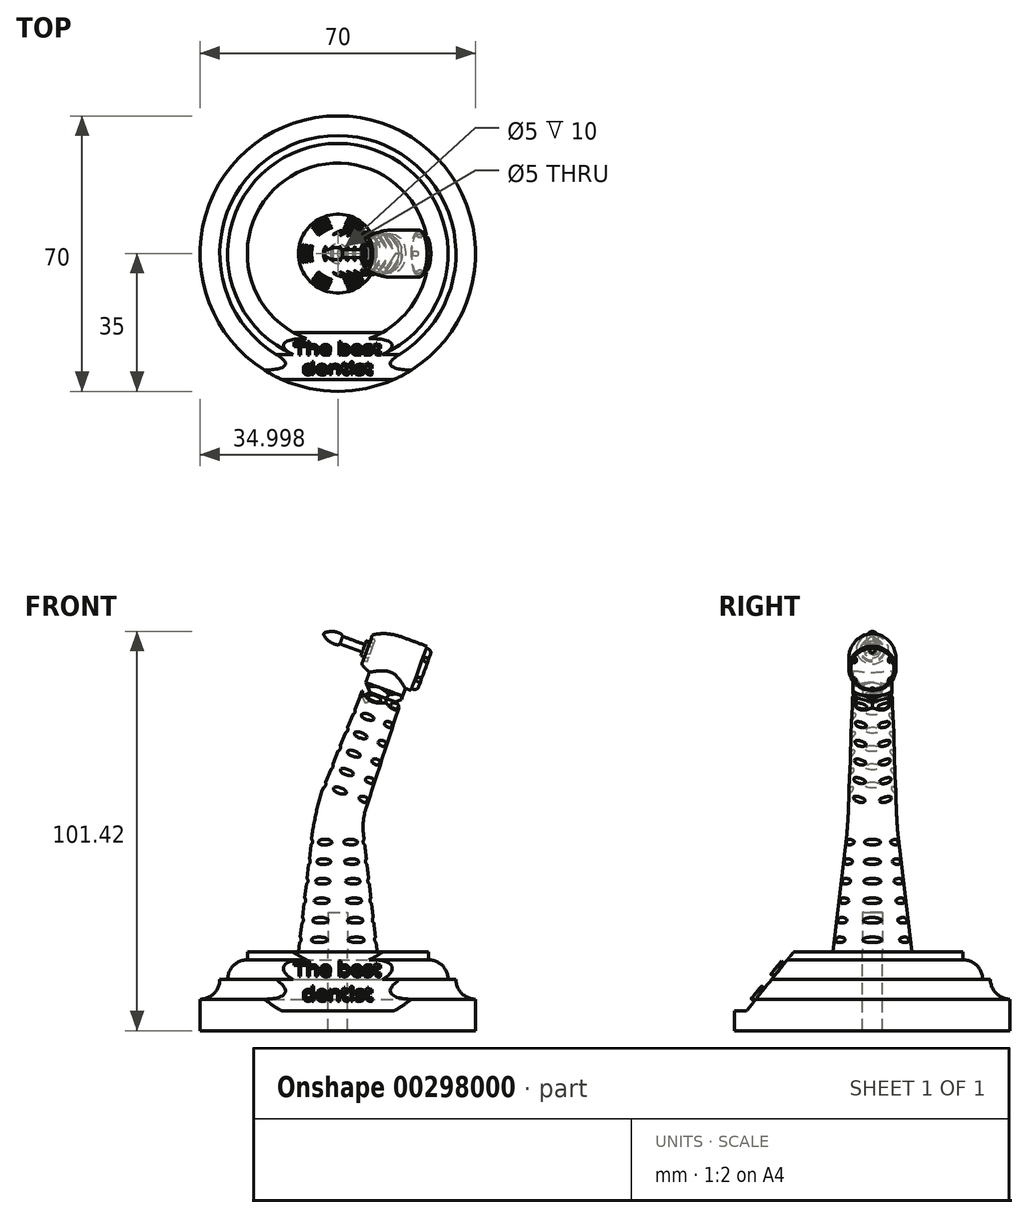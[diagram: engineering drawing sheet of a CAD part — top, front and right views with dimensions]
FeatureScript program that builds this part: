
annotation { "Feature Type Name" : "Feature", "Feature Type Description" : "" }
export const myFeature = defineFeature(function(context is Context, id is Id, definition is map)
    precondition{}
    {
        {
            var Q0;
            Q0=qCreatedBy(makeId("Front.planeOp"),FACE);
            var sketch = newSketch(context, id + "F0", { "sketchPlane" : qUnion([Q0])});
            skLineSegment(sketch, "E0.top", {"start": v(0, 6) * mm, "end": v(-7.07, 6) * mm});
            skArc(sketch, "E1", {"start": v(-7.07, 6) * mm, "mid": v(-10.68, 5.49) * mm, "end": v(-14, 4) * mm});
            skLineSegment(sketch, "E2", {"start": v(0, 6) * mm, "end": v(0, 0) * mm});
            skLineSegment(sketch, "E3", {"start": v(-14, 4) * mm, "end": v(-14, 3) * mm});
            skLineSegment(sketch, "E4", {"start": v(-13, 0) * mm, "end": v(0, 0) * mm});
            skLineSegment(sketch, "E5", {"start": v(0, 5.5) * mm, "end": v(0.5, 5.5) * mm});
            skLineSegment(sketch, "E6", {"start": v(1.5, 4.5) * mm, "end": v(1.5, 0) * mm});
            skPoint(sketch, "E7.visualSharp", {"position": v(1.5, 5.5) * mm});
            skArc(sketch, "E7.filletArc", {"start": v(1.5, 4.5) * mm, "mid": v(1.2, 5.2) * mm, "end": v(0.5, 5.5) * mm});
            skLineSegment(sketch, "E8", {"start": v(1.5, 0) * mm, "end": v(0, 0) * mm});
            skLineSegment(sketch, "E9", {"start": v(-14, 3) * mm, "end": v(-13, 3) * mm});
            skLineSegment(sketch, "E10", {"start": v(-13, 3) * mm, "end": v(-13, 2) * mm});
            skLineSegment(sketch, "E11", {"start": v(-13, 2) * mm, "end": v(-15, 2) * mm});
            skLineSegment(sketch, "E12", {"start": v(-15, 2) * mm, "end": v(-15, 1) * mm});
            skLineSegment(sketch, "E13", {"start": v(-15, 1) * mm, "end": v(-13, 1) * mm});
            skLineSegment(sketch, "E14", {"start": v(-13, 1) * mm, "end": v(-13, 0) * mm});
            skLineSegment(sketch, "E15", {"start": v(-25.15, 0) * mm, "end": v(8.44, 0) * mm, "construction": true});
            skLineSegment(sketch, "E16", {"start": v(-6.5, 17.79) * mm, "end": v(-6.5, -18.93) * mm, "construction": true});
            skSolve(sketch);
        }
        {
            var Q0;
            {var subQ1=sQuery(id+"F0.wireOp",EDGE,"E0.top");Q0=makeQuery(id+"F0.imprint","IMPRINT",FACE,{"disambiguationData":[TD([[makeQuery(id+"F0.imprint","IMPRINT",EDGE,{"derivedFrom":subQ1}),1.0]])]});}
            var Q1;
            Q1=sQuery(id+"F0.wireOp",EDGE,"E15");
            revolve(context, id + "F1", {"entities" : qUnion([Q0]), "axis" : qUnion([Q1]), "revolveType" : RevolveType.FULL});
        }
        {
            var Q0;
            {var subQ0=sQuery(id+"F0.wireOp",EDGE,"E5");Q0=makeQuery(id+"F0.imprint","IMPRINT",FACE,{"disambiguationData":[TD([[makeQuery(id+"F0.imprint","IMPRINT",EDGE,{"derivedFrom":subQ0}),-1.0]])]});}
            var Q1;
            Q1=sQuery(id+"F0.wireOp",EDGE,"E15");
            revolve(context, id + "F2", {"entities" : qUnion([Q0]), "axis" : qUnion([Q1]), "revolveType" : RevolveType.FULL});
        }
        {
            var Q0;
            Q0=qCreatedBy(makeId("Front.planeOp"),FACE);
            var sketch = newSketch(context, id + "F3", { "sketchPlane" : qUnion([Q0])});
            skLineSegment(sketch, "E17", {"start": v(11.5, 0) * mm, "end": v(-3.06, 8.57) * mm, "construction": true});
            skArc(sketch, "E18.0", {"start": v(1.5, 4.5) * mm, "mid": v(1.2, 5.2) * mm, "end": v(0.5, 5.5) * mm, "construction": true});
            skLineSegment(sketch, "E19", {"start": v(0.5, 7.63) * mm, "end": v(3.95, 5.6) * mm});
            skLineSegment(sketch, "E20", {"start": v(3.95, 5.6) * mm, "end": v(3.45, 4.74) * mm});
            skLineSegment(sketch, "E21", {"start": v(3.45, 4.74) * mm, "end": v(0, 6.77) * mm});
            skLineSegment(sketch, "E22", {"start": v(0, 6.77) * mm, "end": v(0.5, 7.63) * mm});
            skSolve(sketch);
        }
        {
            var Q0;
            Q0 = qSketchRegion(id + "F3", true);
            var Q1;
            Q1=sQuery(id+"F3.wireOp",EDGE,"E17");
            revolve(context, id + "F4", {"entities" : qUnion([Q0]), "axis" : qUnion([Q1]), "revolveType" : RevolveType.FULL});
        }
        {
            var Q0;
            Q0=makeQuery(id+"F4.opRevolve","SWEPT_BODY",BODY,{"disambiguationData":[OSD([sQuery(id+"F3.wireOp",EDGE,"E19"),sQuery(id+"F3.wireOp",EDGE,"E20"),sQuery(id+"F3.wireOp",EDGE,"E21"),sQuery(id+"F3.wireOp",EDGE,"E22")])]});
            var Q1;
            Q1=sQuery(id+"F0.wireOp",EDGE,"E15");
            circularPattern(context, id + "F5", {"entities" : qUnion([Q0]), "axis" : qUnion([Q1]), "angle" : 360 * degree, "instanceCount" : 6, "equalSpace" : true});
        }
        {
            var Q0;
            Q0=makeQuery(id+"F4.opRevolve","SWEPT_BODY",BODY,{"disambiguationData":[OSD([sQuery(id+"F3.wireOp",EDGE,"E19"),sQuery(id+"F3.wireOp",EDGE,"E20"),sQuery(id+"F3.wireOp",EDGE,"E21"),sQuery(id+"F3.wireOp",EDGE,"E22")])]});
            var Q1;
            Q1=makeQuery(id+"F5.opPattern","COPY",BODY,{"derivedFrom":makeQuery(id+"F4.opRevolve","SWEPT_BODY",BODY,{"disambiguationData":[OSD([sQuery(id+"F3.wireOp",EDGE,"E19"),sQuery(id+"F3.wireOp",EDGE,"E20"),sQuery(id+"F3.wireOp",EDGE,"E21"),sQuery(id+"F3.wireOp",EDGE,"E22")])]}),"instanceName":"4"});
            var Q2;
            Q2=makeQuery(id+"F5.opPattern","COPY",BODY,{"derivedFrom":makeQuery(id+"F4.opRevolve","SWEPT_BODY",BODY,{"disambiguationData":[OSD([sQuery(id+"F3.wireOp",EDGE,"E19"),sQuery(id+"F3.wireOp",EDGE,"E20"),sQuery(id+"F3.wireOp",EDGE,"E21"),sQuery(id+"F3.wireOp",EDGE,"E22")])]}),"instanceName":"3"});
            var Q3;
            Q3=makeQuery(id+"F5.opPattern","COPY",BODY,{"derivedFrom":makeQuery(id+"F4.opRevolve","SWEPT_BODY",BODY,{"disambiguationData":[OSD([sQuery(id+"F3.wireOp",EDGE,"E19"),sQuery(id+"F3.wireOp",EDGE,"E20"),sQuery(id+"F3.wireOp",EDGE,"E21"),sQuery(id+"F3.wireOp",EDGE,"E22")])]}),"instanceName":"2"});
            var Q4;
            Q4=makeQuery(id+"F5.opPattern","COPY",BODY,{"derivedFrom":makeQuery(id+"F4.opRevolve","SWEPT_BODY",BODY,{"disambiguationData":[OSD([sQuery(id+"F3.wireOp",EDGE,"E19"),sQuery(id+"F3.wireOp",EDGE,"E20"),sQuery(id+"F3.wireOp",EDGE,"E21"),sQuery(id+"F3.wireOp",EDGE,"E22")])]}),"instanceName":"1"});
            var Q5;
            Q5=makeQuery(id+"F5.opPattern","COPY",BODY,{"derivedFrom":makeQuery(id+"F4.opRevolve","SWEPT_BODY",BODY,{"disambiguationData":[OSD([sQuery(id+"F3.wireOp",EDGE,"E19"),sQuery(id+"F3.wireOp",EDGE,"E20"),sQuery(id+"F3.wireOp",EDGE,"E21"),sQuery(id+"F3.wireOp",EDGE,"E22")])]}),"instanceName":"5"});
            var Q6;
            Q6=makeQuery(id+"F2.opRevolve","SWEPT_BODY",BODY,{"disambiguationData":[OSD([sQuery(id+"F0.wireOp",EDGE,"E2"),sQuery(id+"F0.wireOp",EDGE,"E5"),sQuery(id+"F0.wireOp",EDGE,"E6"),sQuery(id+"F0.wireOp",EDGE,"E7.filletArc"),sQuery(id+"F0.wireOp",EDGE,"E8")])]});
            booleanBodies(context, id + "F6", {"operationType" : BooleanOperationType.SUBTRACTION, "tools" : qUnion([Q0, Q1, Q2, Q3, Q4, Q5]), "targets" : qUnion([Q6])});
        }
        {
            var Q0;
            Q0=qCreatedBy(makeId("Front.planeOp"),FACE);
            var sketch = newSketch(context, id + "F7", { "sketchPlane" : qUnion([Q0])});
            skLineSegment(sketch, "E23.0", {"start": v(-25.15, 0) * mm, "end": v(8.44, 0) * mm, "construction": true});
            skPoint(sketch, "E24.0", {"position": v(-13, 1) * mm});
            skLineSegment(sketch, "E25", {"start": v(-13, 1) * mm, "end": v(-21, 1) * mm});
            skArc(sketch, "E26", {"start": v(-21.74, 1.5) * mm, "mid": v(-23.76, 1.33) * mm, "end": v(-25.55, 0.39) * mm});
            skArc(sketch, "E27", {"start": v(-21, 1) * mm, "mid": v(-21.31, 1.33) * mm, "end": v(-21.74, 1.5) * mm});
            skArc(sketch, "E28", {"start": v(-25.55, 0.39) * mm, "mid": v(-25.69, 0.21) * mm, "end": v(-25.73, 0) * mm});
            skLineSegment(sketch, "E29", {"start": v(-25.73, 0) * mm, "end": v(-13, 0) * mm});
            skLineSegment(sketch, "E30", {"start": v(-13, 0) * mm, "end": v(-13, 1) * mm});
            skSolve(sketch);
        }
        {
            var Q0;
            Q0 = qSketchRegion(id + "F7", true);
            var Q1;
            Q1=sQuery(id+"F7.wireOp",EDGE,"E23.0");
            revolve(context, id + "F8", {"entities" : qUnion([Q0]), "axis" : qUnion([Q1]), "revolveType" : RevolveType.FULL});
        }
        {
            var Q0;
            Q0=qCreatedBy(makeId("Top.planeOp"),FACE);
            cPlane(context, id + "F9", {"entities" : qUnion([Q0]), "cplaneType" : CPlaneType.OFFSET, "offset" : 6 * mm, "oppositeDirection" : true, "width" : 150 * mm, "height" : 150 * mm});
        }
        {
            var Q0;
            Q0=qCreatedBy(id+"F9.planeOp",FACE);
            var sketch = newSketch(context, id + "F10", { "sketchPlane" : qUnion([Q0])});
            skPoint(sketch, "E31.0", {"position": v(-6.5, 0) * mm});
            skCircle(sketch, "E32", {"center": v(-6.5, 0) * mm, "radius": 5 * mm});
            skSolve(sketch);
        }
        {
            var Q0;
            Q0 = qSketchRegion(id + "F10", true);
            extrude(context, id + "F11", {"entities" : qUnion([Q0]), "operationType" : NewBodyOperationType.ADD, "depth" : 5 * mm, "hasSecondDirection" : true, "secondDirectionOppositeDirection" : true, "secondDirectionDepth" : 2 * mm});
        }
        {
            var Q0;
            Q0=qCreatedBy(makeId("Front.planeOp"),FACE);
            var sketch = newSketch(context, id + "F12", { "sketchPlane" : qUnion([Q0])});
            skLineSegment(sketch, "E33", {"start": v(-6.5, 12.02) * mm, "end": v(-6.5, -38) * mm, "construction": true});
            skLineSegment(sketch, "E34", {"start": v(-11.5, -8) * mm, "end": v(-12.5, -38) * mm});
            skLineSegment(sketch, "E35.0", {"start": v(-11.5, -8) * mm, "end": v(-1.5, -8) * mm});
            skLineSegment(sketch, "E36", {"start": v(-6.5, -38) * mm, "end": v(-6.5, -8) * mm});
            skLineSegment(sketch, "E37", {"start": v(-12.5, -38) * mm, "end": v(-0.5, -38) * mm});
            skLineSegment(sketch, "E38", {"start": v(-5, -46.55) * mm, "end": v(38.76, -166.76) * mm, "construction": true});
            skLineSegment(sketch, "E39", {"start": v(5.27, -74.74) * mm, "end": v(-4.13, -78.16) * mm});
            skLineSegment(sketch, "E40", {"start": v(-11.1, -48.77) * mm, "end": v(1.12, -44.33) * mm});
            skPoint(sketch, "E41", {"position": v(-5, -46.55) * mm});
            skLineSegment(sketch, "E42", {"start": v(-11.1, -48.77) * mm, "end": v(-4.13, -78.16) * mm});
            skLineSegment(sketch, "E43", {"start": v(-5, -46.55) * mm, "end": v(5.27, -74.74) * mm});
            skArc(sketch, "E44", {"start": v(-6.5, -38) * mm, "mid": v(-6.12, -42.34) * mm, "end": v(-5, -46.55) * mm});
            skSolve(sketch);
        }
        {
            var Q0;
            {var subQ0=sQuery(id+"F12.wireOp",EDGE,"E34");Q0=makeQuery(id+"F12.imprint","IMPRINT",FACE,{"disambiguationData":[TD([[makeQuery(id+"F12.imprint","IMPRINT",EDGE,{"derivedFrom":subQ0}),1.0]])]});}
            var Q1;
            Q1=sQuery(id+"F12.wireOp",EDGE,"E33");
            revolve(context, id + "F13", {"operationType" : NewBodyOperationType.ADD, "entities" : qUnion([Q0]), "axis" : qUnion([Q1]), "revolveType" : RevolveType.FULL});
        }
        {
            var Q0;
            Q0=makeQuery(id+"F12.imprint","IMPRINT",FACE,{"disambiguationData":[TD([[makeQuery(id+"F12.imprint","IMPRINT",EDGE,{"derivedFrom":sQuery(id+"F12.wireOp",EDGE,"E39")}),-1.0]])]});
            var Q1;
            Q1=makeQuery(id+"F12.imprint","IMPRINT",FACE,{"disambiguationData":[TD([[makeQuery(id+"F12.imprint","IMPRINT",EDGE,{"derivedFrom":sQuery(id+"F12.wireOp",EDGE,"E39")}),1.0]])]});
            var Q2;
            Q2=sQuery(id+"F12.wireOp",EDGE,"E38");
            revolve(context, id + "F14", {"entities" : qUnion([Q0, Q1]), "axis" : qUnion([Q2]), "revolveType" : RevolveType.FULL});
        }
        {
            var Q2;
            Q2=makeQuery(id+"F13.opRevolve","SWEPT_FACE",FACE,{"disambiguationData":[OSD([sQuery(id+"F12.wireOp",EDGE,"E37")])]});
            var Q3;
            Q3=makeQuery(id+"F14.opRevolve","SWEPT_FACE",FACE,{"disambiguationData":[OSD([sQuery(id+"F12.wireOp",EDGE,"E40")])]});
            loft(context, id + "F15", {"operationType" : NewBodyOperationType.ADD, "startCondition" : LoftEndDerivativeType.MATCH_TANGENT, "startMagnitude" : 1, "endCondition" : LoftEndDerivativeType.MATCH_TANGENT, "endMagnitude" : 1, "sheetProfilesArray" : [{ "sheetProfileEntities" : qUnion([Q2]) }, { "sheetProfileEntities" : qUnion([Q3]) }]});
        }
        {
            var Q0;
            Q0=qCreatedBy(makeId("Front.planeOp"),FACE);
            var sketch = newSketch(context, id + "F16", { "sketchPlane" : qUnion([Q0])});
            skLineSegment(sketch, "E45.0", {"start": v(-11.5, -8) * mm, "end": v(-12.5, -38) * mm, "construction": true});
            skLineSegment(sketch, "E45.1", {"start": v(-11.1, -48.77) * mm, "end": v(-4.13, -78.16) * mm, "construction": true});
            skLineSegment(sketch, "E46", {"start": v(-12.16, -6.94) * mm, "end": v(-13.27, -40.1) * mm, "construction": true});
            skCircle(sketch, "E47", {"center": v(-13.13, -36) * mm, "radius": 1 * mm});
            skCircle(sketch, "E48", {"center": v(-12.97, -31) * mm, "radius": 1 * mm});
            skCircle(sketch, "E49", {"center": v(-12.8, -26) * mm, "radius": 1 * mm});
            skCircle(sketch, "E50", {"center": v(-12.63, -21) * mm, "radius": 1 * mm});
            skLineSegment(sketch, "E51", {"start": v(-11.5, -8) * mm, "end": v(-9.57, -10) * mm});
            skLineSegment(sketch, "E52", {"start": v(-9.57, -10) * mm, "end": v(-11.63, -12) * mm});
            skLineSegment(sketch, "E53", {"start": v(-11.63, -12) * mm, "end": v(-11.5, -8) * mm});
            skCircle(sketch, "E54", {"center": v(-12.47, -16.01) * mm, "radius": 1 * mm});
            skLineSegment(sketch, "E55", {"start": v(-12.52, -45.84) * mm, "end": v(-4.54, -79.46) * mm, "construction": true});
            skCircle(sketch, "E56", {"center": v(-11.3, -50.97) * mm, "radius": 1 * mm});
            skCircle(sketch, "E57", {"center": v(-10.14, -55.84) * mm, "radius": 1 * mm});
            skCircle(sketch, "E58", {"center": v(-8.99, -60.7) * mm, "radius": 1 * mm});
            skCircle(sketch, "E59", {"center": v(-7.84, -65.57) * mm, "radius": 1 * mm});
            skCircle(sketch, "E60", {"center": v(-6.68, -70.43) * mm, "radius": 1 * mm});
            skCircle(sketch, "E61", {"center": v(-5.53, -75.3) * mm, "radius": 1 * mm});
            skCircle(sketch, "E62", {"center": v(-12.3, -11.01) * mm, "radius": 1 * mm});
            skSolve(sketch);
        }
        {
            var Q0;
            {var subQ1=sQuery(id+"F16.wireOp",EDGE,"E51");Q0=makeQuery(id+"F16.imprint","IMPRINT",FACE,{"disambiguationData":[TD([[makeQuery(id+"F16.imprint","IMPRINT",EDGE,{"derivedFrom":subQ1}),-1.0]])]});}
            var Q1;
            {var subQ0=sQuery(id+"F16.wireOp",EDGE,"E62");var subQ1=sQuery(id+"F16.wireOp",EDGE,"E53");var subQ2=makeQuery(id+"F16.imprint","INTERSECT",VERTEX,{"disambiguationData":[OD(0.0)],"derivedFrom":[subQ1,subQ0]});Q1=makeQuery(id+"F16.imprint","IMPRINT",FACE,{"disambiguationData":[TD([[makeQuery(id+"F16.imprint","IMPRINT",EDGE,{"disambiguationData":[TD([[subQ2,-1.0]])],"derivedFrom":subQ1}),-1.0]])]});}
            extrude(context, id + "F17", {"entities" : qUnion([Q0, Q1]), "operationType" : NewBodyOperationType.REMOVE, "endBound" : BoundingType.SYMMETRIC, "oppositeDirection" : true, "depth" : 25 * mm});
        }
        {
            var Q0;
            Q0=makeQuery(id+"F16.imprint","IMPRINT",FACE,{"disambiguationData":[TD([[makeQuery(id+"F16.imprint","IMPRINT",EDGE,{"derivedFrom":sQuery(id+"F16.wireOp",EDGE,"E54")}),1.0]])]});
            var Q1;
            Q1=makeQuery(id+"F16.imprint","IMPRINT",FACE,{"disambiguationData":[TD([[makeQuery(id+"F16.imprint","IMPRINT",EDGE,{"derivedFrom":sQuery(id+"F16.wireOp",EDGE,"E50")}),1.0]])]});
            var Q2;
            Q2=makeQuery(id+"F16.imprint","IMPRINT",FACE,{"disambiguationData":[TD([[makeQuery(id+"F16.imprint","IMPRINT",EDGE,{"derivedFrom":sQuery(id+"F16.wireOp",EDGE,"E49")}),1.0]])]});
            var Q3;
            Q3=makeQuery(id+"F16.imprint","IMPRINT",FACE,{"disambiguationData":[TD([[makeQuery(id+"F16.imprint","IMPRINT",EDGE,{"derivedFrom":sQuery(id+"F16.wireOp",EDGE,"E48")}),1.0]])]});
            var Q4;
            Q4=makeQuery(id+"F16.imprint","IMPRINT",FACE,{"disambiguationData":[TD([[makeQuery(id+"F16.imprint","IMPRINT",EDGE,{"derivedFrom":sQuery(id+"F16.wireOp",EDGE,"E47")}),1.0]])]});
            var Q5;
            Q5=makeQuery(id+"F16.imprint","IMPRINT",FACE,{"disambiguationData":[TD([[makeQuery(id+"F16.imprint","IMPRINT",EDGE,{"derivedFrom":sQuery(id+"F16.wireOp",EDGE,"E56")}),1.0]])]});
            var Q6;
            Q6=makeQuery(id+"F16.imprint","IMPRINT",FACE,{"disambiguationData":[TD([[makeQuery(id+"F16.imprint","IMPRINT",EDGE,{"derivedFrom":sQuery(id+"F16.wireOp",EDGE,"E57")}),1.0]])]});
            var Q7;
            Q7=makeQuery(id+"F16.imprint","IMPRINT",FACE,{"disambiguationData":[TD([[makeQuery(id+"F16.imprint","IMPRINT",EDGE,{"derivedFrom":sQuery(id+"F16.wireOp",EDGE,"E58")}),1.0]])]});
            var Q8;
            Q8=makeQuery(id+"F16.imprint","IMPRINT",FACE,{"disambiguationData":[TD([[makeQuery(id+"F16.imprint","IMPRINT",EDGE,{"derivedFrom":sQuery(id+"F16.wireOp",EDGE,"E59")}),1.0]])]});
            var Q9;
            Q9=makeQuery(id+"F16.imprint","IMPRINT",FACE,{"disambiguationData":[TD([[makeQuery(id+"F16.imprint","IMPRINT",EDGE,{"derivedFrom":sQuery(id+"F16.wireOp",EDGE,"E60")}),1.0]])]});
            var Q10;
            Q10=makeQuery(id+"F16.imprint","IMPRINT",FACE,{"disambiguationData":[TD([[makeQuery(id+"F16.imprint","IMPRINT",EDGE,{"derivedFrom":sQuery(id+"F16.wireOp",EDGE,"E61")}),1.0]])]});
            var Q11;
            {var subQ0=sQuery(id+"F16.wireOp",EDGE,"E62");var subQ1=sQuery(id+"F16.wireOp",EDGE,"E53");var subQ2=makeQuery(id+"F16.imprint","INTERSECT",VERTEX,{"disambiguationData":[OD(0.0)],"derivedFrom":[subQ1,subQ0]});Q11=makeQuery(id+"F16.imprint","IMPRINT",FACE,{"disambiguationData":[TD([[makeQuery(id+"F16.imprint","IMPRINT",EDGE,{"disambiguationData":[TD([[subQ2,-1.0]])],"derivedFrom":subQ1}),-1.0]])]});}
            var Q12;
            {var subQ0=sQuery(id+"F16.wireOp",EDGE,"E62");var subQ1=sQuery(id+"F16.wireOp",EDGE,"E53");var subQ2=makeQuery(id+"F16.imprint","INTERSECT",VERTEX,{"disambiguationData":[OD(0.0)],"derivedFrom":[subQ1,subQ0]});Q12=makeQuery(id+"F16.imprint","IMPRINT",FACE,{"disambiguationData":[TD([[makeQuery(id+"F16.imprint","IMPRINT",EDGE,{"disambiguationData":[TD([[subQ2,-1.0]])],"derivedFrom":subQ1}),1.0]])]});}
            extrude(context, id + "F18", {"entities" : qUnion([Q0, Q1, Q2, Q3, Q4, Q5, Q6, Q7, Q8, Q9, Q10, Q11, Q12]), "endBound" : BoundingType.SYMMETRIC, "depth" : 25 * mm});
        }
        {
            var Q0;
            Q0=makeQuery(id+"F18.opExtrude","SWEPT_BODY",BODY,{"disambiguationData":[OSD([sQuery(id+"F16.wireOp",EDGE,"E62")])]});
            var Q1;
            Q1=makeQuery(id+"F18.opExtrude","SWEPT_BODY",BODY,{"disambiguationData":[OSD([sQuery(id+"F16.wireOp",EDGE,"E54")])]});
            var Q2;
            Q2=makeQuery(id+"F18.opExtrude","SWEPT_BODY",BODY,{"disambiguationData":[OSD([sQuery(id+"F16.wireOp",EDGE,"E50")])]});
            var Q3;
            Q3=makeQuery(id+"F18.opExtrude","SWEPT_BODY",BODY,{"disambiguationData":[OSD([sQuery(id+"F16.wireOp",EDGE,"E49")])]});
            var Q4;
            Q4=makeQuery(id+"F18.opExtrude","SWEPT_BODY",BODY,{"disambiguationData":[OSD([sQuery(id+"F16.wireOp",EDGE,"E48")])]});
            var Q5;
            Q5=makeQuery(id+"F18.opExtrude","SWEPT_BODY",BODY,{"disambiguationData":[OSD([sQuery(id+"F16.wireOp",EDGE,"E47")])]});
            var Q6;
            Q6=sQuery(id+"F12.wireOp",EDGE,"E33");
            circularPattern(context, id + "F19", {"operationType" : NewBodyOperationType.REMOVE, "entities" : qUnion([Q0, Q1, Q2, Q3, Q4, Q5]), "axis" : qUnion([Q6]), "angle" : 360 * degree, "instanceCount" : 5, "equalSpace" : true});
        }
        {
            var Q0;
            Q0=makeQuery(id+"F18.opExtrude","SWEPT_BODY",BODY,{"disambiguationData":[OSD([sQuery(id+"F16.wireOp",EDGE,"E56")])]});
            var Q1;
            Q1=makeQuery(id+"F18.opExtrude","SWEPT_BODY",BODY,{"disambiguationData":[OSD([sQuery(id+"F16.wireOp",EDGE,"E57")])]});
            var Q2;
            Q2=makeQuery(id+"F18.opExtrude","SWEPT_BODY",BODY,{"disambiguationData":[OSD([sQuery(id+"F16.wireOp",EDGE,"E58")])]});
            var Q3;
            Q3=makeQuery(id+"F18.opExtrude","SWEPT_BODY",BODY,{"disambiguationData":[OSD([sQuery(id+"F16.wireOp",EDGE,"E59")])]});
            var Q4;
            Q4=makeQuery(id+"F18.opExtrude","SWEPT_BODY",BODY,{"disambiguationData":[OSD([sQuery(id+"F16.wireOp",EDGE,"E60")])]});
            var Q5;
            Q5=makeQuery(id+"F18.opExtrude","SWEPT_BODY",BODY,{"disambiguationData":[OSD([sQuery(id+"F16.wireOp",EDGE,"E61")])]});
            var Q6;
            Q6=sQuery(id+"F12.wireOp",EDGE,"E38");
            circularPattern(context, id + "F20", {"operationType" : NewBodyOperationType.REMOVE, "entities" : qUnion([Q0, Q1, Q2, Q3, Q4, Q5]), "axis" : qUnion([Q6]), "angle" : 360 * degree, "instanceCount" : 6, "equalSpace" : true});
        }
        {
            var Q0;
            Q0=makeQuery(id+"F17.boolean.opBoolean","COPY",FACE,{"derivedFrom":makeQuery(id+"F17.opExtrude","SWEPT_FACE",FACE,{"disambiguationData":[OSD([sQuery(id+"F16.wireOp",EDGE,"E52")])]})});
            var sketch = newSketch(context, id + "F21", { "sketchPlane" : qUnion([Q0])});
            skLineSegment(sketch, "E63.0", {"start": v(-13.83, 4.03) * mm, "end": v(-13.83, -4.03) * mm, "construction": true});
            skEllipticalArc(sketch, "E63.1", {"construction": true});
            skLineSegment(sketch, "E64", {"start": v(-13.83, 0) * mm, "end": v(-16.7, 0) * mm, "construction": true});
            skArc(sketch, "E65", {"start": v(-14.52, 0.5) * mm, "mid": v(-15.27, 1.25) * mm, "end": v(-16.02, 0.5) * mm});
            skArc(sketch, "E66", {"start": v(-16.02, -0.5) * mm, "mid": v(-15.27, -1.25) * mm, "end": v(-14.52, -0.5) * mm});
            skPoint(sketch, "E67", {"position": v(-15.27, 0) * mm});
            skLineSegment(sketch, "E68", {"start": v(-16.02, 0.5) * mm, "end": v(-16.02, -0.5) * mm});
            skLineSegment(sketch, "E69", {"start": v(-14.52, 0.5) * mm, "end": v(-14.52, -0.5) * mm});
            const initialGuessF21  = {"E63.1": [-0.009786068873916884, 0, -1, 0, 0.006918582738146398, 0.004970414848461729, 5.336282, 0.9469033072735964]};
            skSetInitialGuess(sketch, initialGuessF21);
            skSolve(sketch);
        }
        {
            var Q0;
            Q0 = qSketchRegion(id + "F21", true);
            extrude(context, id + "F22", {"entities" : qUnion([Q0]), "operationType" : NewBodyOperationType.REMOVE, "oppositeDirection" : true, "depth" : 2 * mm});
        }
        {
            var Q0;
            Q0=makeQuery(id+"F14.opRevolve","SWEPT_FACE",FACE,{"disambiguationData":[OSD([sQuery(id+"F12.wireOp",EDGE,"E39")])]});
            var sketch = newSketch(context, id + "F23", { "sketchPlane" : qUnion([Q0])});
            skCircle(sketch, "E70.0", {"center": v(-20.61, 0) * mm, "radius": 10 * mm});
            skLineSegment(sketch, "E71", {"start": v(-20.61, -10) * mm, "end": v(-20.61, 10) * mm, "construction": true});
            skSolve(sketch);
        }
        {
            var Q0;
            Q0=makeQuery(id+"F1.opRevolve","SWEPT_BODY",BODY,{"disambiguationData":[OSD([sQuery(id+"F0.wireOp",EDGE,"E0.top"),sQuery(id+"F0.wireOp",EDGE,"E1"),sQuery(id+"F0.wireOp",EDGE,"E2"),sQuery(id+"F0.wireOp",EDGE,"E3"),sQuery(id+"F0.wireOp",EDGE,"E4"),sQuery(id+"F0.wireOp",EDGE,"E9"),sQuery(id+"F0.wireOp",EDGE,"E10"),sQuery(id+"F0.wireOp",EDGE,"E11"),sQuery(id+"F0.wireOp",EDGE,"E12"),sQuery(id+"F0.wireOp",EDGE,"E13"),sQuery(id+"F0.wireOp",EDGE,"E14")])]});
            var Q1;
            Q1=makeQuery(id+"F8.opRevolve","SWEPT_BODY",BODY,{"disambiguationData":[OSD([sQuery(id+"F7.wireOp",EDGE,"E25"),sQuery(id+"F7.wireOp",EDGE,"E26"),sQuery(id+"F7.wireOp",EDGE,"E27"),sQuery(id+"F7.wireOp",EDGE,"E28"),sQuery(id+"F7.wireOp",EDGE,"E29"),sQuery(id+"F7.wireOp",EDGE,"E30")])]});
            var Q2;
            Q2=makeQuery(id+"F2.opRevolve","SWEPT_BODY",BODY,{"disambiguationData":[OSD([sQuery(id+"F0.wireOp",EDGE,"E2"),sQuery(id+"F0.wireOp",EDGE,"E5"),sQuery(id+"F0.wireOp",EDGE,"E6"),sQuery(id+"F0.wireOp",EDGE,"E7.filletArc"),sQuery(id+"F0.wireOp",EDGE,"E8")])]});
            var Q3;
            Q3=sQuery(id+"F23.wireOp",EDGE,"E71");
            transform(context, id + "F24", {"entities" : qUnion([Q0, Q1, Q2]), "transformType" : TransformType.ROTATION, "transformAxis" : qUnion([Q3]), "angle" : 20 * degree, "oppositeDirection" : true, "makeCopy" : false});
        }
        {
            var Q0;
            Q0=makeQuery(id+"F14.opRevolve","SWEPT_FACE",FACE,{"disambiguationData":[OSD([sQuery(id+"F12.wireOp",EDGE,"E39")])]});
            var sketch = newSketch(context, id + "F25", { "sketchPlane" : qUnion([Q0])});
            skCircle(sketch, "E72.0", {"center": v(5.27, 0) * mm, "radius": 10 * mm, "construction": true});
            skCircle(sketch, "E73", {"center": v(5.27, 0) * mm, "radius": 28 * mm});
            skCircle(sketch, "E74", {"center": v(5.27, 0) * mm, "radius": 30 * mm});
            skCircle(sketch, "E75", {"center": v(5.27, 0) * mm, "radius": 35 * mm});
            skCircle(sketch, "E76", {"center": v(5.27, 0) * mm, "radius": 2.5 * mm});
            skCircle(sketch, "E77", {"center": v(5.27, 0) * mm, "radius": 23 * mm});
            skSolve(sketch);
        }
        {
            var Q0;
            Q0=makeQuery(id+"F25.imprint","IMPRINT",FACE,{"disambiguationData":[TD([[makeQuery(id+"F25.imprint","IMPRINT",EDGE,{"derivedFrom":sQuery(id+"F25.wireOp",EDGE,"E76")}),1.0]])]});
            extrude(context, id + "F26", {"entities" : qUnion([Q0]), "operationType" : NewBodyOperationType.REMOVE, "oppositeDirection" : true, "depth" : 10 * mm});
        }
        {
            var Q0;
            Q0 = qSketchRegion(id + "F25", true);
            var Q1;
            Q1=makeQuery(id+"F25.imprint","IMPRINT",FACE,{"disambiguationData":[TD([[makeQuery(id+"F25.imprint","IMPRINT",EDGE,{"derivedFrom":sQuery(id+"F25.wireOp",EDGE,"E73")}),1.0]])]});
            var Q2;
            Q2=makeQuery(id+"F25.imprint","IMPRINT",FACE,{"disambiguationData":[TD([[makeQuery(id+"F25.imprint","IMPRINT",EDGE,{"derivedFrom":sQuery(id+"F25.wireOp",EDGE,"E73")}),-1.0]])]});
            var Q3;
            Q3=makeQuery(id+"F25.imprint","IMPRINT",FACE,{"disambiguationData":[TD([[makeQuery(id+"F25.imprint","IMPRINT",EDGE,{"derivedFrom":makeQuery(id+"F14.opRevolve","SWEPT_EDGE",EDGE,{"disambiguationData":[OSD([sQuery(id+"F12.wireOp",EDGE,"E39"),sQuery(id+"F12.wireOp",EDGE,"E42")])]})}),-1.0]])]});
            var Q4;
            Q4=makeQuery(id+"F25.imprint","IMPRINT",FACE,{"disambiguationData":[TD([[makeQuery(id+"F25.imprint","IMPRINT",EDGE,{"derivedFrom":sQuery(id+"F25.wireOp",EDGE,"E77")}),1.0]])]});
            extrude(context, id + "F27", {"entities" : qUnion([Q0, Q1, Q2, Q3, Q4]), "depth" : 20 * mm});
        }
        {
            var Q0;
            Q0=makeQuery(id+"F25.imprint","IMPRINT",FACE,{"disambiguationData":[TD([[makeQuery(id+"F25.imprint","IMPRINT",EDGE,{"derivedFrom":sQuery(id+"F25.wireOp",EDGE,"E73")}),1.0]])]});
            var Q1;
            Q1=makeQuery(id+"F25.imprint","IMPRINT",FACE,{"disambiguationData":[TD([[makeQuery(id+"F25.imprint","IMPRINT",EDGE,{"derivedFrom":sQuery(id+"F25.wireOp",EDGE,"E73")}),-1.0]])]});
            var Q2;
            Q2=makeQuery(id+"F25.imprint","IMPRINT",FACE,{"disambiguationData":[TD([[makeQuery(id+"F25.imprint","IMPRINT",EDGE,{"derivedFrom":sQuery(id+"F25.wireOp",EDGE,"E74")}),-1.0]])]});
            extrude(context, id + "F28", {"entities" : qUnion([Q0, Q1, Q2]), "operationType" : NewBodyOperationType.REMOVE, "depth" : 2 * mm});
        }
        {
            var Q0;
            Q0=makeQuery(id+"F25.imprint","IMPRINT",FACE,{"disambiguationData":[TD([[makeQuery(id+"F25.imprint","IMPRINT",EDGE,{"derivedFrom":sQuery(id+"F25.wireOp",EDGE,"E73")}),-1.0]])]});
            var Q1;
            Q1=makeQuery(id+"F25.imprint","IMPRINT",FACE,{"disambiguationData":[TD([[makeQuery(id+"F25.imprint","IMPRINT",EDGE,{"derivedFrom":sQuery(id+"F25.wireOp",EDGE,"E74")}),-1.0]])]});
            extrude(context, id + "F29", {"entities" : qUnion([Q0, Q1]), "operationType" : NewBodyOperationType.REMOVE, "depth" : 7 * mm});
        }
        {
            var Q0;
            Q0=makeQuery(id+"F25.imprint","IMPRINT",FACE,{"disambiguationData":[TD([[makeQuery(id+"F25.imprint","IMPRINT",EDGE,{"derivedFrom":sQuery(id+"F25.wireOp",EDGE,"E74")}),-1.0]])]});
            extrude(context, id + "F30", {"entities" : qUnion([Q0]), "operationType" : NewBodyOperationType.REMOVE, "depth" : 12 * mm});
        }
        {
            var Q0;
            Q0=makeQuery(id+"F29.boolean.opBoolean","COPY",EDGE,{"derivedFrom":makeQuery(id+"F29.opExtrude","CAP_EDGE",EDGE,{"disambiguationData":[OSD([sQuery(id+"F25.wireOp",EDGE,"E73")])],"isStart":true})});
            var Q1;
            Q1=makeQuery(id+"F29.boolean.opBoolean","INTERSECT",EDGE,{"derivedFrom":[makeQuery(id+"F28.boolean.opBoolean","COPY",FACE,{"derivedFrom":makeQuery(id+"F28.opExtrude","CAP_FACE",FACE,{"disambiguationData":[OSD([sQuery(id+"F25.wireOp",EDGE,"E75"),sQuery(id+"F25.wireOp",EDGE,"E77")])],"isStart":false})}),makeQuery(id+"F29.opExtrude","SWEPT_FACE",FACE,{"disambiguationData":[OSD([sQuery(id+"F25.wireOp",EDGE,"E73")])]})]});
            fillet(context, id + "F31", {"entities" : qUnion([Q0, Q1]), "radius" : 5 * mm, "tangentPropagation" : true, "allowEdgeOverflow" : false});
        }
        {
            var Q0;
            Q0=makeQuery(id+"F30.boolean.opBoolean","COPY",EDGE,{"derivedFrom":makeQuery(id+"F30.opExtrude","CAP_EDGE",EDGE,{"disambiguationData":[OSD([sQuery(id+"F25.wireOp",EDGE,"E74")])],"isStart":false})});
            fillet(context, id + "F32", {"entities" : qUnion([Q0]), "radius" : 5 * mm, "tangentPropagation" : true, "allowEdgeOverflow" : false});
        }
        {
            var Q0;
            Q0=qCreatedBy(makeId("Right.planeOp"),FACE);
            var sketch = newSketch(context, id + "F33", { "sketchPlane" : qUnion([Q0])});
            skLineSegment(sketch, "E78", {"start": v(35, -84.74) * mm, "end": v(35, -94.74) * mm});
            skLineSegment(sketch, "E79", {"start": v(-35, -89.74) * mm, "end": v(-32, -89.74) * mm});
            skLineSegment(sketch, "E80", {"start": v(-32, -89.74) * mm, "end": v(-20, -74.74) * mm});
            skLineSegment(sketch, "E81", {"start": v(-20, -74.74) * mm, "end": v(-35, -74.74) * mm});
            skLineSegment(sketch, "E82", {"start": v(-35, -74.74) * mm, "end": v(-35, -89.74) * mm});
            skLineSegment(sketch, "E83.0", {"start": v(35, -74.74) * mm, "end": v(-35, -74.74) * mm, "construction": true});
            skSolve(sketch);
        }
        {
            var Q0;
            Q0 = qSketchRegion(id + "F33", true);
            extrude(context, id + "F34", {"entities" : qUnion([Q0]), "operationType" : NewBodyOperationType.REMOVE, "endBound" : BoundingType.SYMMETRIC, "depth" : 80 * mm});
        }
        {
            var Q0;
            Q0=makeQuery(id+"F34.boolean.opBoolean","COPY",FACE,{"derivedFrom":makeQuery(id+"F34.opExtrude","SWEPT_FACE",FACE,{"disambiguationData":[OSD([sQuery(id+"F33.wireOp",EDGE,"E80")])]})});
            var sketch = newSketch(context, id + "F35", { "sketchPlane" : qUnion([Q0])});
            skText(sketch, "E84", { "text": "The best", "fontName": "OpenSans-Regular.ttf"});
            skText(sketch, "E85", { "text": "dentist", "fontName": "OpenSans-Regular.ttf"});
            skFitSpline(sketch, "E86.0", {"points": [v(-6.07, -79.82) * mm, v(-6.4, -79.58) * mm, v(-7.04, -79.07) * mm, v(-7.66, -78.4) * mm, v(-8, -77.88) * mm, v(-8.16, -77.62) * mm, v(-8.3, -77.34) * mm, v(-8.45, -76.96) * mm, v(-8.54, -76.56) * mm, v(-8.56, -76.15) * mm, v(-8.53, -75.84) * mm, v(-8.46, -75.54) * mm, v(-8.34, -75.25) * mm, v(-8.18, -74.99) * mm, v(-7.92, -74.66) * mm, v(-7.6, -74.4) * mm, v(-7.25, -74.19) * mm, v(-6.88, -74) * mm, v(-6.4, -73.83) * mm, v(-5.6, -73.62) * mm, v(-4.6, -73.48) * mm, v(-3.38, -73.42) * mm, v(-2.16, -73.42) * mm, v(-0.94, -73.45) * mm, v(0.69, -73.51) * mm, v(2.72, -73.6) * mm, v(5.17, -73.64) * mm, v(7.61, -73.6) * mm, v(9.65, -73.52) * mm, v(11.28, -73.46) * mm, v(12.5, -73.42) * mm, v(13.73, -73.41) * mm, v(14.95, -73.47) * mm, v(15.97, -73.6) * mm, v(16.78, -73.78) * mm, v(17.38, -73.98) * mm, v(17.94, -74.26) * mm, v(18.36, -74.58) * mm, v(18.65, -74.89) * mm, v(18.82, -75.15) * mm, v(18.96, -75.43) * mm, v(19.08, -75.83) * mm, v(19.11, -76.36) * mm, v(18.98, -76.99) * mm, v(18.74, -77.56) * mm, v(18.4, -78.1) * mm, v(18.02, -78.59) * mm, v(17.59, -79.03) * mm, v(17.11, -79.45) * mm, v(16.78, -79.7) * mm, v(16.6, -79.82) * mm], "construction": true});
            skEllipticalArc(sketch, "E86.1", {"construction": true});
            skLineSegment(sketch, "E86.2", {"start": v(16.63, -70.86) * mm, "end": v(-6.09, -70.86) * mm, "construction": true});
            skEllipticalArc(sketch, "E86.3", {"construction": true});
            skFitSpline(sketch, "E86.4", {"points": [v(-6.07, -79.82) * mm, v(-6.4, -79.58) * mm, v(-7.04, -79.07) * mm, v(-7.66, -78.4) * mm, v(-8, -77.88) * mm, v(-8.16, -77.62) * mm, v(-8.3, -77.34) * mm, v(-8.45, -76.96) * mm, v(-8.54, -76.56) * mm, v(-8.56, -76.15) * mm, v(-8.53, -75.84) * mm, v(-8.46, -75.54) * mm, v(-8.34, -75.25) * mm, v(-8.18, -74.99) * mm, v(-7.92, -74.66) * mm, v(-7.6, -74.4) * mm, v(-7.25, -74.19) * mm, v(-6.88, -74) * mm, v(-6.4, -73.83) * mm, v(-5.6, -73.62) * mm, v(-4.6, -73.48) * mm, v(-3.38, -73.42) * mm, v(-2.16, -73.42) * mm, v(-0.94, -73.45) * mm, v(0.69, -73.51) * mm, v(2.72, -73.6) * mm, v(5.17, -73.64) * mm, v(7.61, -73.6) * mm, v(9.65, -73.52) * mm, v(11.28, -73.46) * mm, v(12.5, -73.42) * mm, v(13.73, -73.41) * mm, v(14.95, -73.47) * mm, v(15.97, -73.6) * mm, v(16.78, -73.78) * mm, v(17.38, -73.98) * mm, v(17.94, -74.26) * mm, v(18.36, -74.58) * mm, v(18.65, -74.89) * mm, v(18.82, -75.15) * mm, v(18.96, -75.43) * mm, v(19.08, -75.83) * mm, v(19.11, -76.36) * mm, v(18.98, -76.99) * mm, v(18.74, -77.56) * mm, v(18.4, -78.1) * mm, v(18.02, -78.59) * mm, v(17.59, -79.03) * mm, v(17.11, -79.45) * mm, v(16.78, -79.7) * mm, v(16.6, -79.82) * mm], "construction": true});
            skLineSegment(sketch, "E86.5", {"start": v(20.9, -79.82) * mm, "end": v(16.61, -79.82) * mm, "construction": true});
            skFitSpline(sketch, "E86.6", {"points": [v(36, -79.82) * mm, v(35.76, -80.3) * mm, v(35.32, -80.96) * mm, v(34.65, -81.76) * mm, v(34.1, -82.33) * mm, v(33.5, -82.86) * mm, v(32.67, -83.5) * mm, v(31.8, -84.08) * mm, v(30.86, -84.58) * mm, v(29.9, -85.03) * mm, v(28.67, -85.5) * mm, v(27.15, -85.9) * mm, v(25.58, -86.16) * mm, v(24.26, -86.24) * mm, v(23.21, -86.21) * mm, v(22.42, -86.14) * mm, v(21.63, -86.02) * mm, v(20.87, -85.83) * mm, v(20.12, -85.55) * mm, v(19.53, -85.22) * mm, v(19.13, -84.87) * mm, v(18.87, -84.57) * mm, v(18.68, -84.22) * mm, v(18.57, -83.83) * mm, v(18.56, -83.42) * mm, v(18.65, -82.9) * mm, v(18.91, -82.28) * mm, v(19.33, -81.6) * mm, v(19.82, -80.98) * mm, v(20.35, -80.38) * mm, v(20.72, -80) * mm, v(20.9, -79.82) * mm], "construction": true});
            skEllipticalArc(sketch, "E86.7", {"construction": true});
            skLineSegment(sketch, "E86.8", {"start": v(19.45, -90.07) * mm, "end": v(-8.9, -90.07) * mm, "construction": true});
            skEllipticalArc(sketch, "E86.9", {"construction": true});
            skFitSpline(sketch, "E86.10", {"points": [v(-10.37, -79.82) * mm, v(-10.18, -80) * mm, v(-9.8, -80.39) * mm, v(-9.28, -80.98) * mm, v(-8.79, -81.62) * mm, v(-8.44, -82.18) * mm, v(-8.21, -82.67) * mm, v(-8.09, -83.05) * mm, v(-8.02, -83.45) * mm, v(-8.04, -83.78) * mm, v(-8.1, -84.04) * mm, v(-8.16, -84.23) * mm, v(-8.24, -84.41) * mm, v(-8.39, -84.64) * mm, v(-8.6, -84.89) * mm, v(-9.02, -85.23) * mm, v(-9.6, -85.55) * mm, v(-10.35, -85.83) * mm, v(-11.12, -86.02) * mm, v(-11.9, -86.15) * mm, v(-12.7, -86.21) * mm, v(-13.74, -86.24) * mm, v(-15.05, -86.16) * mm, v(-16.35, -85.94) * mm, v(-17.38, -85.7) * mm, v(-18.39, -85.4) * mm, v(-19.61, -84.93) * mm, v(-20.79, -84.35) * mm, v(-21.7, -83.8) * mm, v(-22.56, -83.2) * mm, v(-23.37, -82.53) * mm, v(-24.1, -81.77) * mm, v(-24.79, -80.96) * mm, v(-25.22, -80.3) * mm, v(-25.47, -79.82) * mm], "construction": true});
            skLineSegment(sketch, "E86.11", {"start": v(-6.07, -79.82) * mm, "end": v(-10.37, -79.82) * mm, "construction": true});
            skLineSegment(sketch, "E87", {"start": v(5.27, -70.86) * mm, "end": v(5.27, -90.07) * mm, "construction": true});
            const initialGuessF35  = {"E84": [-0.00594, -0.07886, 1, 0, 0.004], "E85": [-0.0038, -0.08686, 1, 0, 0.004], "E86.1": [0.005268288780122365, -0.038841415816930416, 0, 1, 0.03681796436523888, 0.023, 2.6251175127429187, 2.790886775477257], "E86.3": [0.005268288780122365, -0.038841415816930416, 0, 1, 0.03681796436523888, 0.023, 3.4922985317023154, 3.6580677944366675], "E86.7": [0.005268288780122365, -0.038841415816930416, 0, 1, 0.05602733707753744, 0.035, 3.558647947875568, 3.7044868098221664], "E86.9": [0.005268288780122365, -0.038841415816930416, 0, 1, 0.05602733707753744, 0.035, 2.578698603724565, 2.724537359304018]};
            skSetInitialGuess(sketch, initialGuessF35);
            skSolve(sketch);
        }
        {
            var Q0;
            Q0 = qSketchRegion(id + "F35", true);
            extrude(context, id + "F36", {"entities" : qUnion([Q0]), "operationType" : NewBodyOperationType.ADD, "depth" : 1 * mm});
        }
    });
